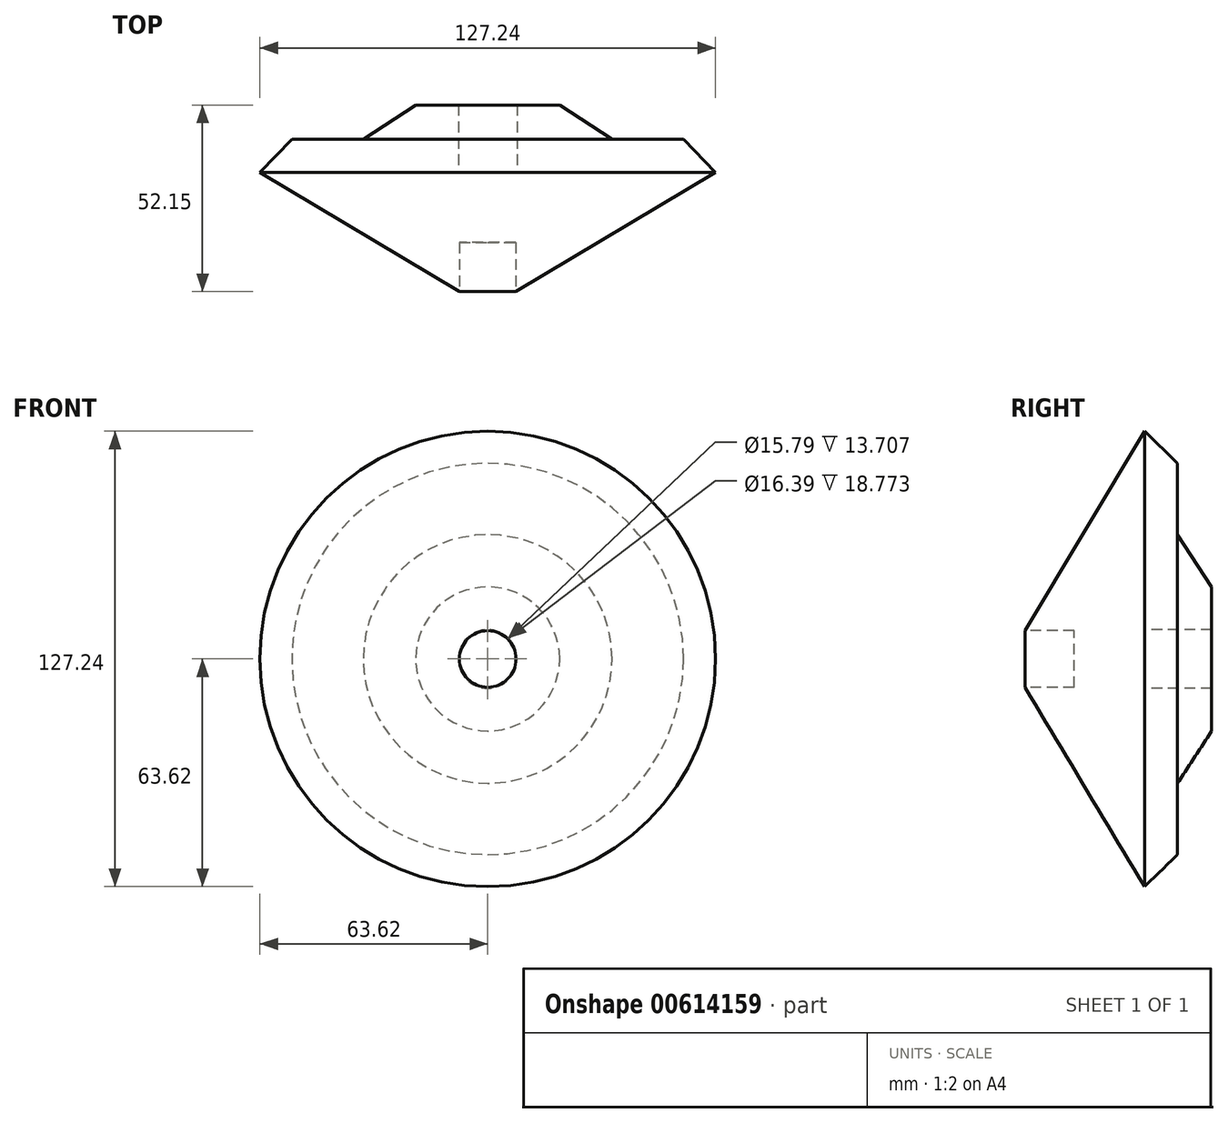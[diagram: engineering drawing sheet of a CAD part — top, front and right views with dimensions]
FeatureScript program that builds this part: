
annotation { "Feature Type Name" : "Feature", "Feature Type Description" : "" }
export const myFeature = defineFeature(function(context is Context, id is Id, definition is map)
    precondition{}
    {
        {
            var Q0;
            Q0=qCreatedBy(makeId("Top.planeOp"),FACE);
            var sketch = newSketch(context, id + "F0", { "sketchPlane" : qUnion([Q0])});
            skLineSegment(sketch, "E0", {"start": v(7.9, 0) * mm, "end": v(7.9, 13.7) * mm});
            skLineSegment(sketch, "E1", {"start": v(7.9, 13.7) * mm, "end": v(0, 13.7) * mm});
            skLineSegment(sketch, "E2", {"start": v(0, 13.7) * mm, "end": v(0, 33.37) * mm});
            skLineSegment(sketch, "E3", {"start": v(0, 33.37) * mm, "end": v(8.2, 33.37) * mm});
            skLineSegment(sketch, "E4", {"start": v(8.2, 33.37) * mm, "end": v(8.2, 52.15) * mm});
            skLineSegment(sketch, "E5", {"start": v(8.2, 52.15) * mm, "end": v(20.11, 52.15) * mm});
            skLineSegment(sketch, "E6", {"start": v(20.11, 52.15) * mm, "end": v(34.72, 42.61) * mm});
            skLineSegment(sketch, "E7", {"start": v(34.72, 42.61) * mm, "end": v(54.68, 42.61) * mm});
            skLineSegment(sketch, "E8", {"start": v(54.68, 42.61) * mm, "end": v(63.62, 33.37) * mm});
            skLineSegment(sketch, "E9", {"start": v(63.62, 33.37) * mm, "end": v(7.9, 0) * mm});
            skSolve(sketch);
        }
        {
            var Q0;
            Q0=makeQuery(id+"F0.imprint","IMPRINT",FACE,{"disambiguationData":[TD([[makeQuery(id+"F0.imprint","IMPRINT",EDGE,{"derivedFrom":sQuery(id+"F0.wireOp",EDGE,"E0")}),-1.0]])]});
            var Q1;
            Q1=sQuery(id+"F0.wireOp",EDGE,"E2");
            revolve(context, id + "F1", {"entities" : qUnion([Q0]), "axis" : qUnion([Q1]), "revolveType" : RevolveType.FULL});
        }
    });
